FCSTD DOCUMENT  (FreeCAD 1.0R39319 (Git))
Label: DielectricShieldedPair
License: All rights reserved
LicenseURL: https://en.wikipedia.org/wiki/All_rights_reserved
objects: Part::Part2DObjectPython×5, App::DocumentObjectGroupPython×3, App::FeaturePython×2, App::DocumentObjectGroup×2
note: 5 computed .brp shape members not serialized (recipe doc carries the construction recipe); baked Part::Feature solids carry a one-line shape summary decoded from their .brp

FEATURE [App::FeaturePython] PECMaterial  label="PEC"  # WARN: FeaturePython — macro-defined, semantics opaque (R4)
FEATURE [Part::Part2DObjectPython] Circle001  label="LeftConductor"  # Draft 2D object (typed FeaturePython)
  Area = 201.062
  FirstAngle = 0
  LastAngle = 0
  MakeFace = true
  Material = -> PECMaterial
  Placement = pos=(-20,0,0) rot=(0,0,1;0rad)
  Radius = 8
FEATURE [Part::Part2DObjectPython] Circle  label="ExternalShield"  # Draft 2D object (typed FeaturePython)
  Area = 7853.98
  FirstAngle = 0
  LastAngle = 0
  MakeFace = true
  Material = -> PECMaterial
  Radius = 50
FEATURE [Part::Part2DObjectPython] Circle003  label="RightConductor"  # Draft 2D object (typed FeaturePython)
  Area = 201.062
  FirstAngle = 0
  LastAngle = 0
  MakeFace = true
  Material = -> PECMaterial
  Placement = pos=(20,0,0) rot=(0,0,1;0rad)
  Radius = 8
FEATURE [App::DocumentObjectGroup] Group  label="Conductors"
  Group = -> [Circle003,Circle,Circle001]
FEATURE [App::FeaturePython] DielectricMaterial  label="Dielectric Material"  # WARN: FeaturePython — macro-defined, semantics opaque (R4)
FEATURE [Part::Part2DObjectPython] Circle002  label="LeftDielectric"  # Draft 2D object (typed FeaturePython)
  Area = 804.248
  FirstAngle = 0
  LastAngle = 0
  MakeFace = true
  Material = -> DielectricMaterial
  Placement = pos=(-20,0,0) rot=(0,0,1;0rad)
  Radius = 16
FEATURE [Part::Part2DObjectPython] Circle004  label="RightDielectric"  # Draft 2D object (typed FeaturePython)
  Area = 804.248
  FirstAngle = 0
  LastAngle = 0
  MakeFace = true
  Material = -> DielectricMaterial
  Placement = pos=(20,0,0) rot=(0,0,1;0rad)
  Radius = 16
FEATURE [App::DocumentObjectGroupPython] MaterialGroup  label="Materials"  # scripted group (container) (typed FeaturePython)
  Group = -> [PECMaterial,DielectricMaterial]
FEATURE [App::DocumentObjectGroup] Group001  label="Dielectric"
  Group = -> [Circle004,Circle002]
FEATURE [App::DocumentObjectGroupPython] CaseStudy  label="Model"  # scripted group (container) (typed FeaturePython)
  Group = -> [Group,Group001]
FEATURE [App::DocumentObjectGroupPython] CrossSection  label="Cross-Section"  # scripted group (container) (typed FeaturePython)
  Group = -> [MaterialGroup,CaseStudy]
